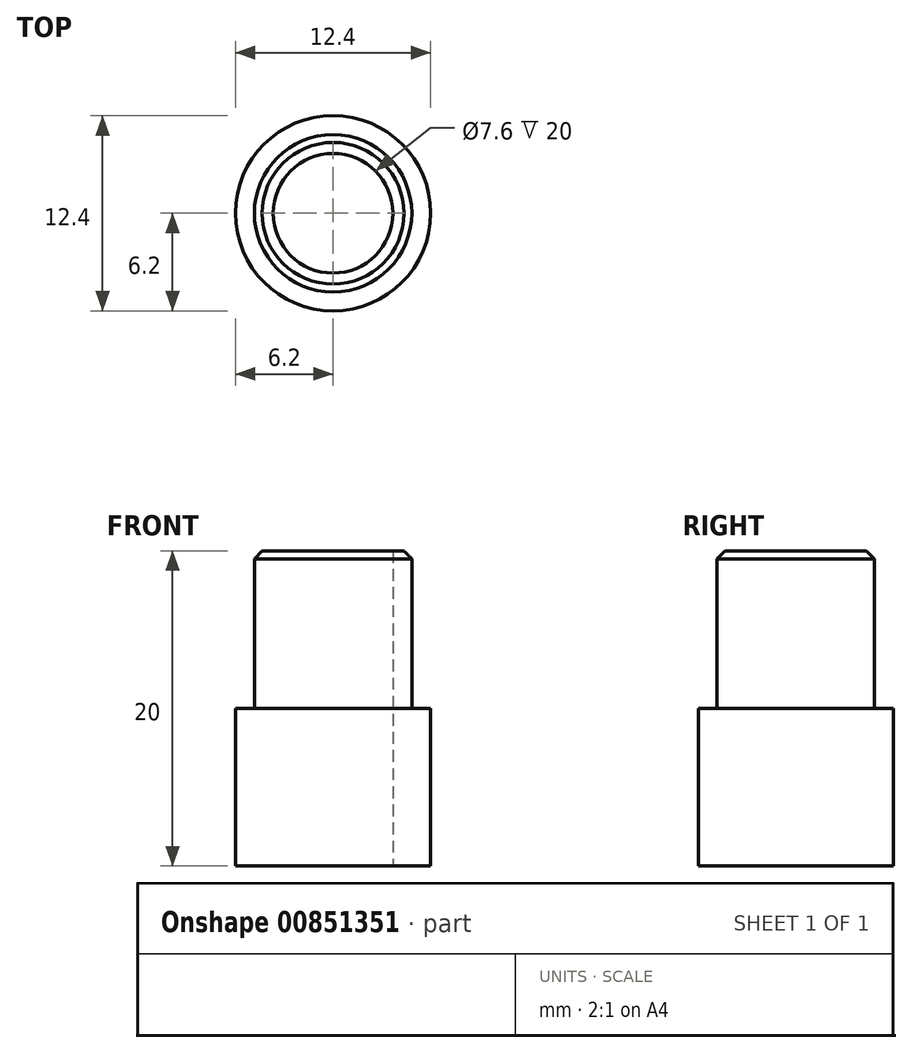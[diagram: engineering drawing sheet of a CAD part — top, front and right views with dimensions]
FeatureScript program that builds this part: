
annotation { "Feature Type Name" : "Feature", "Feature Type Description" : "" }
export const myFeature = defineFeature(function(context is Context, id is Id, definition is map)
    precondition{}
    {
        {
            var Q0;
            Q0=qCreatedBy(makeId("Top.planeOp"),FACE);
            var sketch = newSketch(context, id + "F0", { "sketchPlane" : qUnion([Q0])});
            skCircle(sketch, "E0", {"center": v(0, 0) * mm, "radius": 6.2 * mm});
            skCircle(sketch, "E1", {"center": v(0, 0) * mm, "radius": 5 * mm});
            skCircle(sketch, "E2", {"center": v(0, 0) * mm, "radius": 3.8 * mm});
            skSolve(sketch);
        }
        {
            var Q0;
            Q0 = qSketchRegion(id + "F0", true);
            extrude(context, id + "F1", {"entities" : qUnion([Q0]), "depth" : 10 * mm, "offsetDistance" : 25 * mm});
        }
        {
            var Q0;
            Q0=makeQuery(id+"F0.imprint","IMPRINT",FACE,{"disambiguationData":[TD([[makeQuery(id+"F0.imprint","IMPRINT",EDGE,{"derivedFrom":sQuery(id+"F0.wireOp",EDGE,"E1")}),1.0]])]});
            extrude(context, id + "F2", {"entities" : qUnion([Q0]), "operationType" : NewBodyOperationType.ADD, "depth" : 20 * mm, "offsetDistance" : 25 * mm});
        }
        {
            var Q0;
            Q0=makeQuery(id+"F2.opExtrude","CAP_EDGE",EDGE,{"disambiguationData":[OSD([sQuery(id+"F0.wireOp",EDGE,"E1")])],"isStart":false});
            chamfer(context, id + "F3", {"entities" : qUnion([Q0]), "width" : 0.5 * mm, "tangentPropagation" : true});
        }
    });
